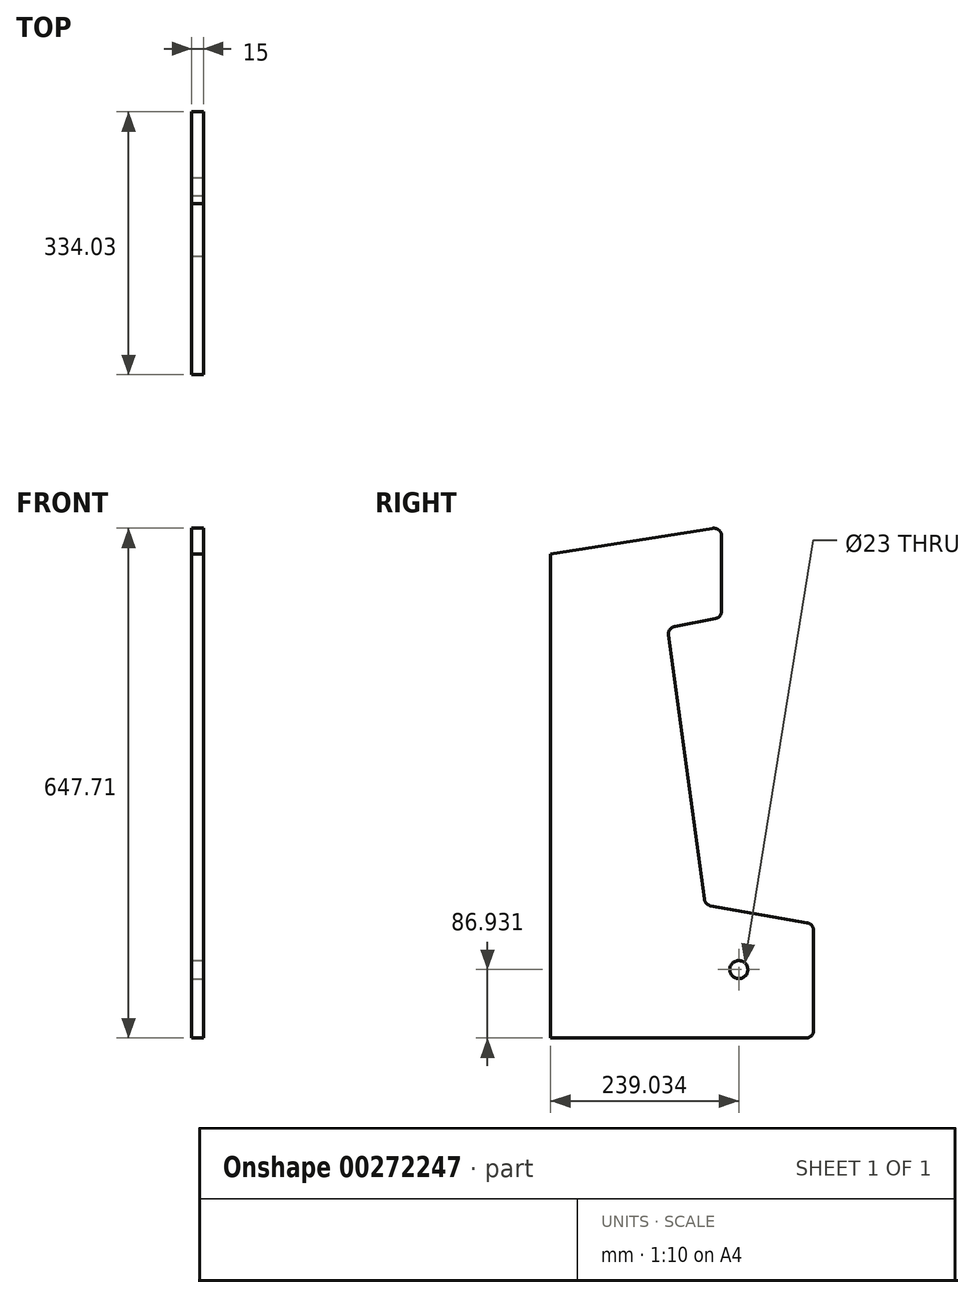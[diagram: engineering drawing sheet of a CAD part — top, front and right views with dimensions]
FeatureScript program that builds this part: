
annotation { "Feature Type Name" : "Feature", "Feature Type Description" : "" }
export const myFeature = defineFeature(function(context is Context, id is Id, definition is map)
    precondition{}
    {
        {
            var Q0;
            Q0=qCreatedBy(makeId("Front.planeOp"),FACE);
            var sketch = newSketch(context, id + "F0", { "sketchPlane" : qUnion([Q0])});
            skLineSegment(sketch, "E0", {"start": v(252.58, -100.88) * mm, "end": v(-81.45, -100.88) * mm});
            skLineSegment(sketch, "E1", {"start": v(-81.45, -100.88) * mm, "end": v(-81.45, 44.12) * mm});
            skLineSegment(sketch, "E2", {"start": v(-81.45, 44.12) * mm, "end": v(56.42, 68.43) * mm});
            skLineSegment(sketch, "E3", {"start": v(56.42, 68.43) * mm, "end": v(104.03, 420.3) * mm});
            skLineSegment(sketch, "E4", {"start": v(104.03, 420.3) * mm, "end": v(35.3, 433.54) * mm});
            skLineSegment(sketch, "E5", {"start": v(35.3, 433.54) * mm, "end": v(35.3, 548.54) * mm});
            skLineSegment(sketch, "E6", {"start": v(35.3, 548.54) * mm, "end": v(252.58, 514.12) * mm});
            skLineSegment(sketch, "E7", {"start": v(252.58, 514.12) * mm, "end": v(252.58, -100.88) * mm});
            skPoint(sketch, "E8", {"position": v(248.44, -103.01) * mm});
            skPoint(sketch, "E9", {"position": v(252.58, 504.12) * mm});
            skCircle(sketch, "E10", {"center": v(13.55, -13.95) * mm, "radius": 11.5 * mm});
            skSolve(sketch);
        }
        {
            var Q0;
            Q0 = qSketchRegion(id + "F0", true);
            extrude(context, id + "F1", {"entities" : qUnion([Q0]), "offsetDistance" : 25 * mm, "depth" : 15 * mm});
        }
        {
            var Q0;
            Q0=makeQuery(id+"F1.opExtrude","SWEPT_BODY",BODY,{"disambiguationData":[OSD([sQuery(id+"F0.wireOp",EDGE,"E0"),sQuery(id+"F0.wireOp",EDGE,"E1"),sQuery(id+"F0.wireOp",EDGE,"E2"),sQuery(id+"F0.wireOp",EDGE,"E3"),sQuery(id+"F0.wireOp",EDGE,"E4"),sQuery(id+"F0.wireOp",EDGE,"E5"),sQuery(id+"F0.wireOp",EDGE,"E6"),sQuery(id+"F0.wireOp",EDGE,"E7")])]});
            var Q1;
            Q1=makeQuery(id+"F1.opExtrude","CAP_EDGE",EDGE,{"disambiguationData":[OSD([sQuery(id+"F0.wireOp",EDGE,"E7")])],"isStart":false});
            transform(context, id + "F2", {"entities" : qUnion([Q0]), "transformType" : TransformType.ROTATION, "transformAxis" : qUnion([Q1]), "angle" : 90 * degree, "makeCopy" : false});
        }
        {
            var Q0;
            Q0=makeQuery(id+"F1.opExtrude","SWEPT_EDGE",EDGE,{"disambiguationData":[OSD([sQuery(id+"F0.wireOp",EDGE,"E5"),sQuery(id+"F0.wireOp",EDGE,"E6")])]});
            var Q1;
            Q1=makeQuery(id+"F1.opExtrude","SWEPT_EDGE",EDGE,{"disambiguationData":[OSD([sQuery(id+"F0.wireOp",EDGE,"E4"),sQuery(id+"F0.wireOp",EDGE,"E5")])]});
            var Q2;
            Q2=makeQuery(id+"F1.opExtrude","SWEPT_EDGE",EDGE,{"disambiguationData":[OSD([sQuery(id+"F0.wireOp",EDGE,"E3"),sQuery(id+"F0.wireOp",EDGE,"E4")])]});
            var Q3;
            Q3=makeQuery(id+"F1.opExtrude","SWEPT_EDGE",EDGE,{"disambiguationData":[OSD([sQuery(id+"F0.wireOp",EDGE,"E2"),sQuery(id+"F0.wireOp",EDGE,"E3")])]});
            var Q4;
            Q4=makeQuery(id+"F1.opExtrude","SWEPT_EDGE",EDGE,{"disambiguationData":[OSD([sQuery(id+"F0.wireOp",EDGE,"E1"),sQuery(id+"F0.wireOp",EDGE,"E2")])]});
            var Q5;
            Q5=makeQuery(id+"F1.opExtrude","SWEPT_EDGE",EDGE,{"disambiguationData":[OSD([sQuery(id+"F0.wireOp",EDGE,"E0"),sQuery(id+"F0.wireOp",EDGE,"E1")])]});
            fillet(context, id + "F3", {"entities" : qUnion([Q0, Q1, Q2, Q3, Q4, Q5]), "radius" : 10 * mm, "tangentPropagation" : true, "allowEdgeOverflow" : false});
        }
    });
